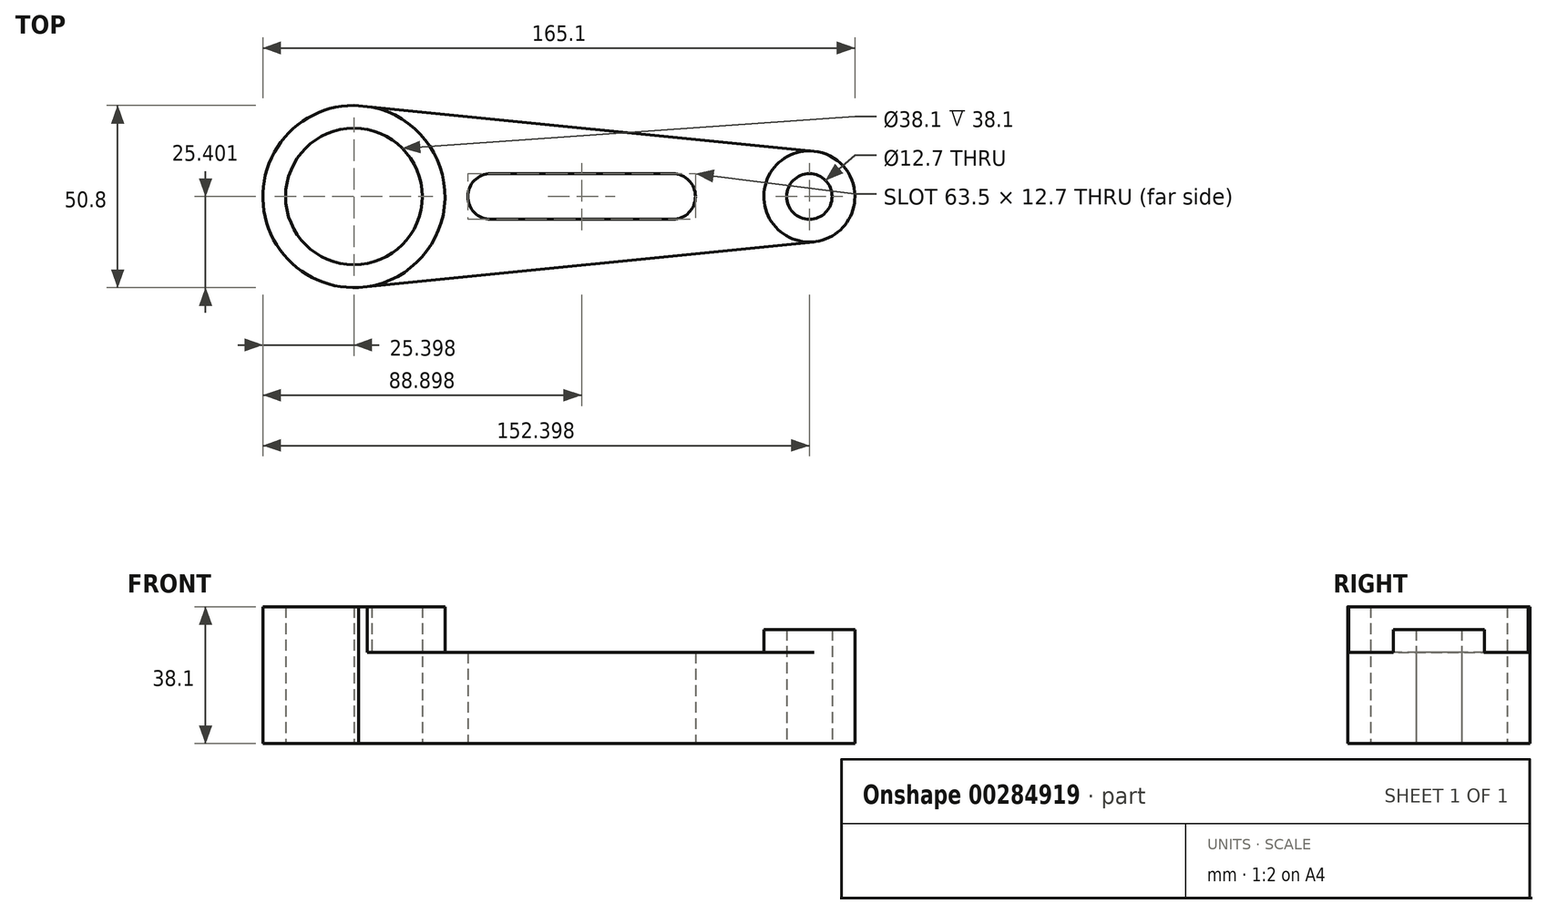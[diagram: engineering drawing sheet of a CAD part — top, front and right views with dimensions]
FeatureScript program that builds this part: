
annotation { "Feature Type Name" : "Feature", "Feature Type Description" : "" }
export const myFeature = defineFeature(function(context is Context, id is Id, definition is map)
    precondition{}
    {
        {
            var Q0;
            Q0=qCreatedBy(makeId("Top.planeOp"),FACE);
            var sketch = newSketch(context, id + "F0", { "sketchPlane" : qUnion([Q0])});
            skCircle(sketch, "E0", {"center": v(-41.37, 15.1) * mm, "radius": 19.05 * mm});
            skCircle(sketch, "E1", {"center": v(-41.37, 15.1) * mm, "radius": 25.4 * mm});
            skCircle(sketch, "E2", {"center": v(85.63, 15.1) * mm, "radius": 6.35 * mm});
            skCircle(sketch, "E3", {"center": v(85.63, 15.1) * mm, "radius": 12.7 * mm});
            skArc(sketch, "E4", {"start": v(-3.27, 21.45) * mm, "mid": v(-9.62, 15.1) * mm, "end": v(-3.27, 8.75) * mm});
            skArc(sketch, "E5", {"start": v(47.53, 8.75) * mm, "mid": v(53.88, 15.1) * mm, "end": v(47.53, 21.45) * mm});
            skLineSegment(sketch, "E6", {"start": v(-3.27, 21.45) * mm, "end": v(47.53, 21.45) * mm});
            skLineSegment(sketch, "E7", {"start": v(-3.27, 8.75) * mm, "end": v(47.53, 8.75) * mm});
            skLineSegment(sketch, "E8", {"start": v(-40.02, -10.26) * mm, "end": v(86.9, 2.46) * mm});
            skLineSegment(sketch, "E9", {"start": v(-41.4, 40.5) * mm, "end": v(86.89, 27.74) * mm});
            skLineSegment(sketch, "E10", {"start": v(-41.37, 15.1) * mm, "end": v(85.63, 15.1) * mm});
            skSolve(sketch);
        }
        {
            var Q0;
            Q0=makeQuery(id+"F0.imprint","IMPRINT",FACE,{"disambiguationData":[TD([[makeQuery(id+"F0.imprint","IMPRINT",EDGE,{"derivedFrom":sQuery(id+"F0.wireOp",EDGE,"E0")}),-1.0]])]});
            extrude(context, id + "F1", {"entities" : qUnion([Q0]), "depth" : 38.1 * mm});
        }
        {
            var Q0;
            Q0=makeQuery(id+"F0.imprint","IMPRINT",FACE,{"disambiguationData":[TD([[makeQuery(id+"F0.imprint","IMPRINT",EDGE,{"derivedFrom":sQuery(id+"F0.wireOp",EDGE,"E4")}),-1.0]])]});
            extrude(context, id + "F2", {"entities" : qUnion([Q0]), "operationType" : NewBodyOperationType.ADD, "depth" : 25.4 * mm});
        }
        {
            var Q0;
            Q0=makeQuery(id+"F0.imprint","IMPRINT",FACE,{"disambiguationData":[TD([[makeQuery(id+"F0.imprint","IMPRINT",EDGE,{"derivedFrom":sQuery(id+"F0.wireOp",EDGE,"E2")}),-1.0]])]});
            extrude(context, id + "F3", {"entities" : qUnion([Q0]), "operationType" : NewBodyOperationType.ADD, "depth" : 31.75 * mm});
        }
    });
